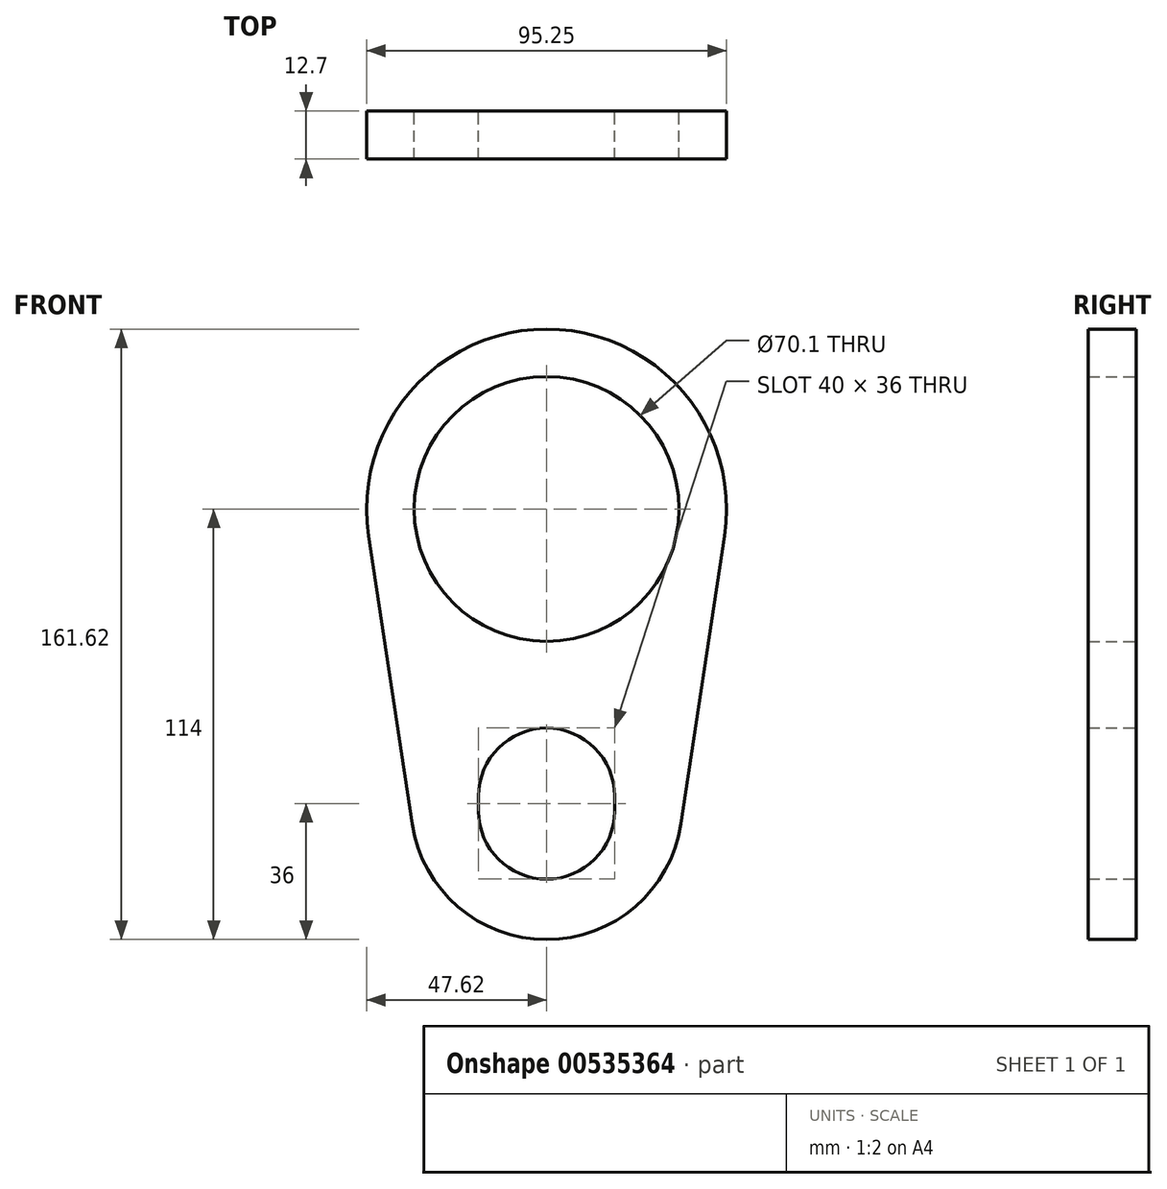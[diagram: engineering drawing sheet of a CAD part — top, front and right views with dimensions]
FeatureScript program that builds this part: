
annotation { "Feature Type Name" : "Feature", "Feature Type Description" : "" }
export const myFeature = defineFeature(function(context is Context, id is Id, definition is map)
    precondition{}
    {
        {
            var Q0;
            Q0=qCreatedBy(makeId("Front.planeOp"),FACE);
            var sketch = newSketch(context, id + "F0", { "sketchPlane" : qUnion([Q0])});
            skArc(sketch, "E0", {"start": v(47.1, -7.1) * mm, "mid": v(0, 47.63) * mm, "end": v(-47.1, -7.1) * mm});
            skLineSegment(sketch, "E1", {"start": v(-47.1, -7.1) * mm, "end": v(-35.6, -83.37) * mm});
            skLineSegment(sketch, "E2", {"start": v(0, 0) * mm, "end": v(0, -78) * mm, "construction": true});
            skLineSegment(sketch, "E3.MirrorCS", {"start": v(47.1, -7.1) * mm, "end": v(35.6, -83.37) * mm});
            skArc(sketch, "E4.trimOffspring", {"start": v(-35.6, -83.37) * mm, "mid": v(0, -114) * mm, "end": v(35.6, -83.37) * mm});
            skCircle(sketch, "E5", {"center": v(0, 0) * mm, "radius": 35.05 * mm});
            skLineSegment(sketch, "E6", {"start": v(0, -76) * mm, "end": v(0, -80) * mm});
            skArc(sketch, "E7.0.startCap", {"start": v(-18, -76) * mm, "mid": v(0, -58) * mm, "end": v(18, -76) * mm});
            skArc(sketch, "E7.0.endCap", {"start": v(18, -80) * mm, "mid": v(0, -98) * mm, "end": v(-18, -80) * mm});
            skLineSegment(sketch, "E7.0.left", {"start": v(18, -76) * mm, "end": v(18, -80) * mm});
            skLineSegment(sketch, "E7.0.right", {"start": v(-18, -76) * mm, "end": v(-18, -80) * mm});
            skSolve(sketch);
        }
        {
            var Q0;
            Q0 = qSketchRegion(id + "F0", true);
            extrude(context, id + "F1", {"entities" : qUnion([Q0]), "depth" : 12.7 * mm, "offsetDistance" : 25.4 * mm});
        }
    });
